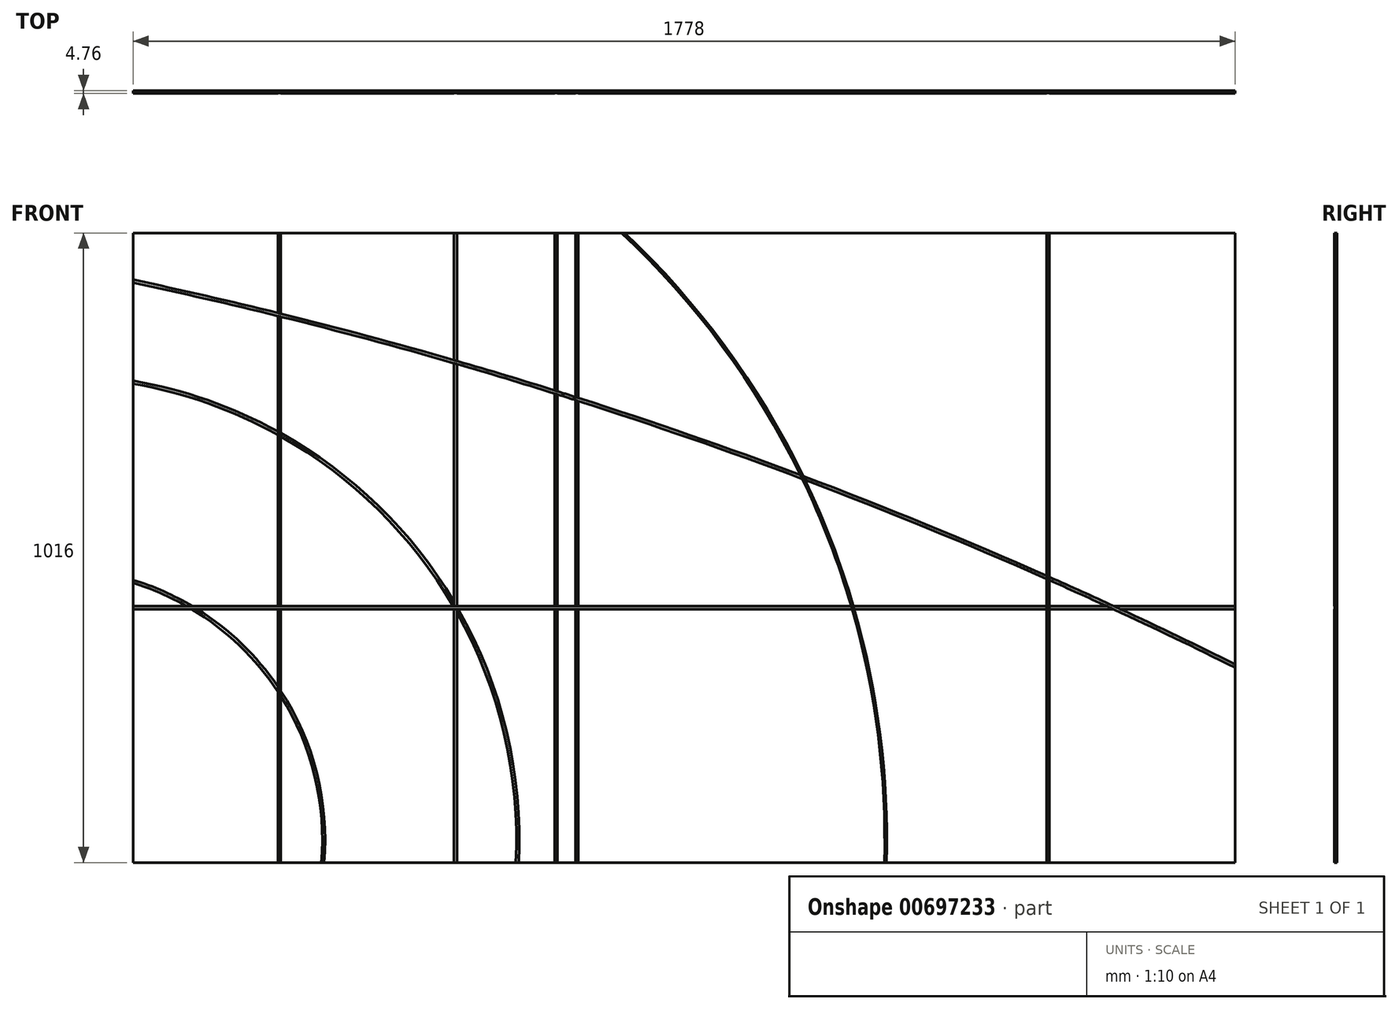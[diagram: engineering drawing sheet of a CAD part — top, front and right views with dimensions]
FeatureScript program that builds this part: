
annotation { "Feature Type Name" : "Feature", "Feature Type Description" : "" }
export const myFeature = defineFeature(function(context is Context, id is Id, definition is map)
    precondition{}
    {
        {
            var Q0;
            Q0=qCreatedBy(makeId("Front.planeOp"),FACE);
            var sketch = newSketch(context, id + "F0", { "sketchPlane" : qUnion([Q0])});
            skLineSegment(sketch, "E0.bottom", {"start": v(889, -508) * mm, "end": v(-889, -508) * mm});
            skLineSegment(sketch, "E0.top", {"start": v(889, 508) * mm, "end": v(-889, 508) * mm});
            skLineSegment(sketch, "E0.left", {"start": v(889, -508) * mm, "end": v(889, 508) * mm});
            skLineSegment(sketch, "E0.right", {"start": v(-889, -508) * mm, "end": v(-889, 508) * mm});
            skPoint(sketch, "E0.middle", {"position": v(0, 0) * mm});
            skSolve(sketch);
        }
        {
            var Q0;
            Q0=makeQuery(id+"F0.imprint","IMPRINT",FACE,{"disambiguationData":[TD([[makeQuery(id+"F0.imprint","IMPRINT",EDGE,{"derivedFrom":sQuery(id+"F0.wireOp",EDGE,"E0.bottom")}),-1.0]])]});
            var sketch = newSketch(context, id + "F1", { "sketchPlane" : qUnion([Q0])});
            skCircle(sketch, "E1", {"center": v(-1017.43, -471) * mm, "radius": 301.1 * mm});
            skCircle(sketch, "E2", {"center": v(-1017.43, -471) * mm, "radius": 434.97 * mm});
            skCircle(sketch, "E3", {"center": v(-1017.43, -471) * mm, "radius": 750 * mm});
            skCircle(sketch, "E4", {"center": v(-1017.43, -471) * mm, "radius": 1344.1 * mm});
            skCircle(sketch, "E5", {"center": v(-2455.27, -6911.53) * mm, "radius": 7513.95 * mm});
            skLineSegment(sketch, "E6.bottom", {"start": v(-1508.25, -953.2) * mm, "end": v(-652.67, -953.2) * mm});
            skLineSegment(sketch, "E6.top", {"start": v(-1508.25, 718.08) * mm, "end": v(-652.67, 718.08) * mm});
            skLineSegment(sketch, "E6.left", {"start": v(-1508.25, -953.2) * mm, "end": v(-1508.25, 718.08) * mm});
            skLineSegment(sketch, "E6.right", {"start": v(-652.67, -953.2) * mm, "end": v(-652.67, 718.08) * mm});
            skLineSegment(sketch, "E7.bottom", {"start": v(-1508.25, -953.2) * mm, "end": v(-368.8, -953.2) * mm});
            skLineSegment(sketch, "E7.top", {"start": v(-1508.25, 815.63) * mm, "end": v(-368.8, 815.63) * mm});
            skLineSegment(sketch, "E7.left", {"start": v(-1508.25, -953.2) * mm, "end": v(-1508.25, 815.63) * mm});
            skLineSegment(sketch, "E7.right", {"start": v(-368.8, -953.2) * mm, "end": v(-368.8, 815.63) * mm});
            skLineSegment(sketch, "E8.bottom", {"start": v(-1508.25, -953.2) * mm, "end": v(1014.94, -953.2) * mm});
            skLineSegment(sketch, "E8.top", {"start": v(-1508.25, -94.8) * mm, "end": v(1014.94, -94.8) * mm});
            skLineSegment(sketch, "E8.left", {"start": v(-1508.25, -953.2) * mm, "end": v(-1508.25, -94.8) * mm});
            skLineSegment(sketch, "E8.right", {"start": v(1014.94, -953.2) * mm, "end": v(1014.94, -94.8) * mm});
            skLineSegment(sketch, "E9.bottom", {"start": v(-1508.25, -953.2) * mm, "end": v(-173.4, -953.2) * mm});
            skLineSegment(sketch, "E9.top", {"start": v(-1508.25, 648.03) * mm, "end": v(-173.4, 648.03) * mm});
            skLineSegment(sketch, "E9.left", {"start": v(-1508.25, -953.2) * mm, "end": v(-1508.25, 648.03) * mm});
            skLineSegment(sketch, "E9.right", {"start": v(-173.4, -953.2) * mm, "end": v(-173.4, 648.03) * mm});
            skCircle(sketch, "E10", {"center": v(-1656.64, -4604.09) * mm, "radius": 5143.5 * mm});
            skLineSegment(sketch, "E11.bottom", {"start": v(-1508.25, -953.2) * mm, "end": v(586.23, -953.2) * mm});
            skLineSegment(sketch, "E11.top", {"start": v(-1508.25, 596.93) * mm, "end": v(586.23, 596.93) * mm});
            skLineSegment(sketch, "E11.left", {"start": v(-1508.25, -953.2) * mm, "end": v(-1508.25, 596.93) * mm});
            skLineSegment(sketch, "E11.right", {"start": v(586.23, -953.2) * mm, "end": v(586.23, 596.93) * mm});
            skLineSegment(sketch, "E12.bottom", {"start": v(-1508.25, -953.2) * mm, "end": v(-206.4, -953.2) * mm});
            skLineSegment(sketch, "E12.top", {"start": v(-1508.25, 550.75) * mm, "end": v(-206.4, 550.75) * mm});
            skLineSegment(sketch, "E12.left", {"start": v(-1508.25, -953.2) * mm, "end": v(-1508.25, 550.75) * mm});
            skLineSegment(sketch, "E12.right", {"start": v(-206.4, -953.2) * mm, "end": v(-206.4, 550.75) * mm});
            skSolve(sketch);
        }
        {
            var Q0;
            Q0 = qSketchRegion(id + "F0", true);
            extrude(context, id + "F2", {"entities" : qUnion([Q0]), "oppositeDirection" : true, "depth" : 4.76 * mm, "offsetDistance" : 25.4 * mm});
        }
        {
            var Q0;
            Q0=makeQuery(id+"F2.opExtrude","SWEPT_FACE",FACE,{"disambiguationData":[OSD([sQuery(id+"F0.wireOp",EDGE,"E0.top")])]});
            var sketch = newSketch(context, id + "F3", { "sketchPlane" : qUnion([Q0])});
            skLineSegment(sketch, "E13.bottom", {"start": v(228.75, -0.8) * mm, "end": v(223.99, -0.8) * mm});
            skLineSegment(sketch, "E13.top", {"start": v(228.75, 0.8) * mm, "end": v(223.99, 0.8) * mm});
            skLineSegment(sketch, "E13.left", {"start": v(228.75, -0.8) * mm, "end": v(228.75, 0.8) * mm});
            skLineSegment(sketch, "E13.right", {"start": v(223.99, -0.8) * mm, "end": v(223.99, 0.8) * mm});
            skPoint(sketch, "E13.middle", {"position": v(226.37, 0) * mm});
            skSolve(sketch);
        }
        {
            var Q0;
            {var subQ1=sQuery(id+"F3.wireOp",EDGE,"E13.top");Q0=makeQuery(id+"F3.imprint","IMPRINT",FACE,{"disambiguationData":[TD([[makeQuery(id+"F3.imprint","IMPRINT",EDGE,{"derivedFrom":subQ1}),-1.0]])]});}
            var sketch = newSketch(context, id + "F4", { "sketchPlane" : qUnion([Q0])});
            skPoint(sketch, "E14", {"position": v(-173.49, 0) * mm});
            skPoint(sketch, "E15", {"position": v(-368.97, 0) * mm});
            skPoint(sketch, "E16", {"position": v(-652.96, 0) * mm});
            skPoint(sketch, "E17", {"position": v(-98.34, 0) * mm});
            skLineSegment(sketch, "E18.bottom", {"start": v(-96.08, -0.16) * mm, "end": v(-100.85, -0.16) * mm});
            skLineSegment(sketch, "E18.top", {"start": v(-96.08, 1.43) * mm, "end": v(-100.85, 1.43) * mm});
            skLineSegment(sketch, "E18.left", {"start": v(-96.08, -0.16) * mm, "end": v(-96.08, 1.43) * mm});
            skLineSegment(sketch, "E18.right", {"start": v(-100.85, -0.16) * mm, "end": v(-100.85, 1.43) * mm});
            skPoint(sketch, "E18.middle", {"position": v(-98.46, 0.63) * mm});
            skLineSegment(sketch, "E19.bottom", {"start": v(-170.65, -0.84) * mm, "end": v(-175.42, -0.84) * mm});
            skLineSegment(sketch, "E19.top", {"start": v(-170.65, 0.75) * mm, "end": v(-175.42, 0.75) * mm});
            skLineSegment(sketch, "E19.left", {"start": v(-170.65, -0.84) * mm, "end": v(-170.65, 0.75) * mm});
            skLineSegment(sketch, "E19.right", {"start": v(-175.42, -0.84) * mm, "end": v(-175.42, 0.75) * mm});
            skPoint(sketch, "E19.middle", {"position": v(-173.03, -0.04) * mm});
            skLineSegment(sketch, "E20.bottom", {"start": v(-366.59, -0.8) * mm, "end": v(-371.35, -0.8) * mm});
            skLineSegment(sketch, "E20.top", {"start": v(-366.59, 0.8) * mm, "end": v(-371.35, 0.8) * mm});
            skLineSegment(sketch, "E20.left", {"start": v(-366.59, -0.8) * mm, "end": v(-366.59, 0.8) * mm});
            skLineSegment(sketch, "E20.right", {"start": v(-371.35, -0.8) * mm, "end": v(-371.35, 0.8) * mm});
            skLineSegment(sketch, "E21.bottom", {"start": v(-650.58, -0.8) * mm, "end": v(-655.34, -0.8) * mm});
            skLineSegment(sketch, "E21.top", {"start": v(-650.58, 0.8) * mm, "end": v(-655.34, 0.8) * mm});
            skLineSegment(sketch, "E21.left", {"start": v(-650.58, -0.8) * mm, "end": v(-650.58, 0.8) * mm});
            skLineSegment(sketch, "E21.right", {"start": v(-655.34, -0.8) * mm, "end": v(-655.34, 0.8) * mm});
            skPoint(sketch, "E22", {"position": v(-207.16, 0.02) * mm});
            skLineSegment(sketch, "E23.bottom", {"start": v(-204.32, -0.81) * mm, "end": v(-209.08, -0.81) * mm});
            skLineSegment(sketch, "E23.top", {"start": v(-204.32, 0.77) * mm, "end": v(-209.08, 0.77) * mm});
            skLineSegment(sketch, "E23.left", {"start": v(-204.32, -0.81) * mm, "end": v(-204.32, 0.77) * mm});
            skLineSegment(sketch, "E23.right", {"start": v(-209.08, -0.81) * mm, "end": v(-209.08, 0.77) * mm});
            skPoint(sketch, "E23.middle", {"position": v(-206.7, -0.02) * mm});
            skPoint(sketch, "E24", {"position": v(587.17, -0.42) * mm});
            skLineSegment(sketch, "E25.bottom", {"start": v(589.43, -0.58) * mm, "end": v(584.67, -0.58) * mm});
            skLineSegment(sketch, "E25.top", {"start": v(589.43, 1) * mm, "end": v(584.67, 1) * mm});
            skLineSegment(sketch, "E25.left", {"start": v(589.43, -0.58) * mm, "end": v(589.43, 1) * mm});
            skLineSegment(sketch, "E25.right", {"start": v(584.67, -0.58) * mm, "end": v(584.67, 1) * mm});
            skPoint(sketch, "E25.middle", {"position": v(587.05, 0.21) * mm});
            skSolve(sketch);
        }
        {
            var Q0;
            Q0=makeQuery(id+"F2.opExtrude","SWEPT_FACE",FACE,{"disambiguationData":[OSD([sQuery(id+"F0.wireOp",EDGE,"E0.right")])]});
            var sketch = newSketch(context, id + "F5", { "sketchPlane" : qUnion([Q0])});
            skPoint(sketch, "E26", {"position": v(0, 429.67) * mm});
            skPoint(sketch, "E27", {"position": v(0, 266.94) * mm});
            skPoint(sketch, "E28", {"position": v(0, -54.83) * mm});
            skPoint(sketch, "E29", {"position": v(0, -97.17) * mm});
            skPoint(sketch, "E30", {"position": v(0, -199.87) * mm});
            skLineSegment(sketch, "E31.bottom", {"start": v(0.8, -197.5) * mm, "end": v(-0.8, -197.5) * mm});
            skLineSegment(sketch, "E31.top", {"start": v(0.8, -202.25) * mm, "end": v(-0.8, -202.25) * mm});
            skLineSegment(sketch, "E31.left", {"start": v(0.8, -197.5) * mm, "end": v(0.8, -202.25) * mm});
            skLineSegment(sketch, "E31.right", {"start": v(-0.8, -197.5) * mm, "end": v(-0.8, -202.25) * mm});
            skPoint(sketch, "E32", {"position": v(-0.1, -96.8) * mm});
            skLineSegment(sketch, "E33.bottom", {"start": v(0.69, -94.42) * mm, "end": v(-0.9, -94.42) * mm});
            skLineSegment(sketch, "E33.top", {"start": v(0.69, -99.18) * mm, "end": v(-0.9, -99.18) * mm});
            skLineSegment(sketch, "E33.left", {"start": v(0.69, -94.42) * mm, "end": v(0.69, -99.18) * mm});
            skLineSegment(sketch, "E33.right", {"start": v(-0.9, -94.42) * mm, "end": v(-0.9, -99.18) * mm});
            skPoint(sketch, "E34", {"position": v(0.14, -54.42) * mm});
            skLineSegment(sketch, "E35.bottom", {"start": v(0.93, -52.04) * mm, "end": v(-0.66, -52.04) * mm});
            skLineSegment(sketch, "E35.top", {"start": v(0.93, -56.8) * mm, "end": v(-0.66, -56.8) * mm});
            skLineSegment(sketch, "E35.left", {"start": v(0.93, -52.04) * mm, "end": v(0.93, -56.8) * mm});
            skLineSegment(sketch, "E35.right", {"start": v(-0.66, -52.04) * mm, "end": v(-0.66, -56.8) * mm});
            skPoint(sketch, "E36", {"position": v(0.08, 267.14) * mm});
            skLineSegment(sketch, "E37.bottom", {"start": v(0.87, 269.52) * mm, "end": v(-0.72, 269.52) * mm});
            skLineSegment(sketch, "E37.top", {"start": v(0.87, 264.75) * mm, "end": v(-0.72, 264.75) * mm});
            skLineSegment(sketch, "E37.left", {"start": v(0.87, 269.52) * mm, "end": v(0.87, 264.75) * mm});
            skLineSegment(sketch, "E37.right", {"start": v(-0.72, 269.52) * mm, "end": v(-0.72, 264.75) * mm});
            skPoint(sketch, "E38", {"position": v(-0.16, 430.13) * mm});
            skLineSegment(sketch, "E39.bottom", {"start": v(0.64, 432.51) * mm, "end": v(-0.95, 432.51) * mm});
            skLineSegment(sketch, "E39.top", {"start": v(0.64, 427.75) * mm, "end": v(-0.95, 427.75) * mm});
            skLineSegment(sketch, "E39.left", {"start": v(0.64, 432.51) * mm, "end": v(0.64, 427.75) * mm});
            skLineSegment(sketch, "E39.right", {"start": v(-0.95, 432.51) * mm, "end": v(-0.95, 427.75) * mm});
            skSolve(sketch);
        }
        {
            var Q0;
            {var subQ0=sQuery(id+"F5.wireOp",EDGE,"E33.right");Q0=makeQuery(id+"F5.imprint","IMPRINT",FACE,{"disambiguationData":[TD([[makeQuery(id+"F5.imprint","IMPRINT",EDGE,{"derivedFrom":subQ0}),1.0]])]});}
            var Q1;
            Q1=sQuery(id+"F1.wireOp",EDGE,"E8.top");
            sweep(context, id + "F6", {"operationType" : NewBodyOperationType.REMOVE, "profiles" : qUnion([Q0]), "path" : qUnion([Q1])});
        }
        {
            var Q0;
            {var subQ0=sQuery(id+"F5.wireOp",EDGE,"E35.right");Q0=makeQuery(id+"F5.imprint","IMPRINT",FACE,{"disambiguationData":[TD([[makeQuery(id+"F5.imprint","IMPRINT",EDGE,{"derivedFrom":subQ0}),1.0]])]});}
            var Q1;
            Q1=sQuery(id+"F1.wireOp",EDGE,"E2");
            sweep(context, id + "F7", {"operationType" : NewBodyOperationType.REMOVE, "profiles" : qUnion([Q0]), "path" : qUnion([Q1])});
        }
        {
            var Q0;
            {var subQ0=sQuery(id+"F5.wireOp",EDGE,"E37.right");Q0=makeQuery(id+"F5.imprint","IMPRINT",FACE,{"disambiguationData":[TD([[makeQuery(id+"F5.imprint","IMPRINT",EDGE,{"derivedFrom":subQ0}),1.0]])]});}
            var Q1;
            Q1=sQuery(id+"F1.wireOp",EDGE,"E3");
            sweep(context, id + "F8", {"operationType" : NewBodyOperationType.REMOVE, "profiles" : qUnion([Q0]), "path" : qUnion([Q1])});
        }
        {
            var Q0;
            {var subQ0=sQuery(id+"F5.wireOp",EDGE,"E39.right");Q0=makeQuery(id+"F5.imprint","IMPRINT",FACE,{"disambiguationData":[TD([[makeQuery(id+"F5.imprint","IMPRINT",EDGE,{"derivedFrom":subQ0}),1.0]])]});}
            var Q1;
            Q1=sQuery(id+"F1.wireOp",EDGE,"E5");
            sweep(context, id + "F9", {"operationType" : NewBodyOperationType.REMOVE, "profiles" : qUnion([Q0]), "path" : qUnion([Q1])});
        }
        {
            var Q0;
            {var subQ0=sQuery(id+"F4.wireOp",EDGE,"E21.top");Q0=makeQuery(id+"F4.imprint","IMPRINT",FACE,{"disambiguationData":[TD([[makeQuery(id+"F4.imprint","IMPRINT",EDGE,{"derivedFrom":subQ0}),1.0]])]});}
            var Q1;
            {var subQ0=sQuery(id+"F4.wireOp",EDGE,"E20.top");Q1=makeQuery(id+"F4.imprint","IMPRINT",FACE,{"disambiguationData":[TD([[makeQuery(id+"F4.imprint","IMPRINT",EDGE,{"derivedFrom":subQ0}),1.0]])]});}
            var Q2;
            {var subQ0=sQuery(id+"F4.wireOp",EDGE,"E19.top");Q2=makeQuery(id+"F4.imprint","IMPRINT",FACE,{"disambiguationData":[TD([[makeQuery(id+"F4.imprint","IMPRINT",EDGE,{"derivedFrom":subQ0}),1.0]])]});}
            var Q3;
            Q3=sQuery(id+"F1.wireOp",EDGE,"E6.right");
            sweep(context, id + "F10", {"operationType" : NewBodyOperationType.REMOVE, "profiles" : qUnion([Q0, Q1, Q2]), "path" : qUnion([Q3])});
        }
        {
            var Q0;
            {var subQ0=sQuery(id+"F4.wireOp",EDGE,"E18.top");Q0=makeQuery(id+"F4.imprint","IMPRINT",FACE,{"disambiguationData":[TD([[makeQuery(id+"F4.imprint","IMPRINT",EDGE,{"derivedFrom":subQ0}),1.0]])]});}
            var Q1;
            Q1=sQuery(id+"F1.wireOp",EDGE,"E4");
            sweep(context, id + "F11", {"operationType" : NewBodyOperationType.REMOVE, "profiles" : qUnion([Q0]), "path" : qUnion([Q1])});
        }
        {
            var Q0;
            {var subQ0=sQuery(id+"F4.wireOp",EDGE,"E23.top");Q0=makeQuery(id+"F4.imprint","IMPRINT",FACE,{"disambiguationData":[TD([[makeQuery(id+"F4.imprint","IMPRINT",EDGE,{"derivedFrom":subQ0}),1.0]])]});}
            var Q1;
            Q1=sQuery(id+"F1.wireOp",EDGE,"E12.right");
            sweep(context, id + "F12", {"operationType" : NewBodyOperationType.REMOVE, "profiles" : qUnion([Q0]), "path" : qUnion([Q1])});
        }
        {
            var Q0;
            {var subQ0=sQuery(id+"F4.wireOp",EDGE,"E25.top");Q0=makeQuery(id+"F4.imprint","IMPRINT",FACE,{"disambiguationData":[TD([[makeQuery(id+"F4.imprint","IMPRINT",EDGE,{"derivedFrom":subQ0}),1.0]])]});}
            var Q1;
            Q1=sQuery(id+"F1.wireOp",EDGE,"E11.right");
            sweep(context, id + "F13", {"operationType" : NewBodyOperationType.REMOVE, "profiles" : qUnion([Q0]), "path" : qUnion([Q1])});
        }
    });
